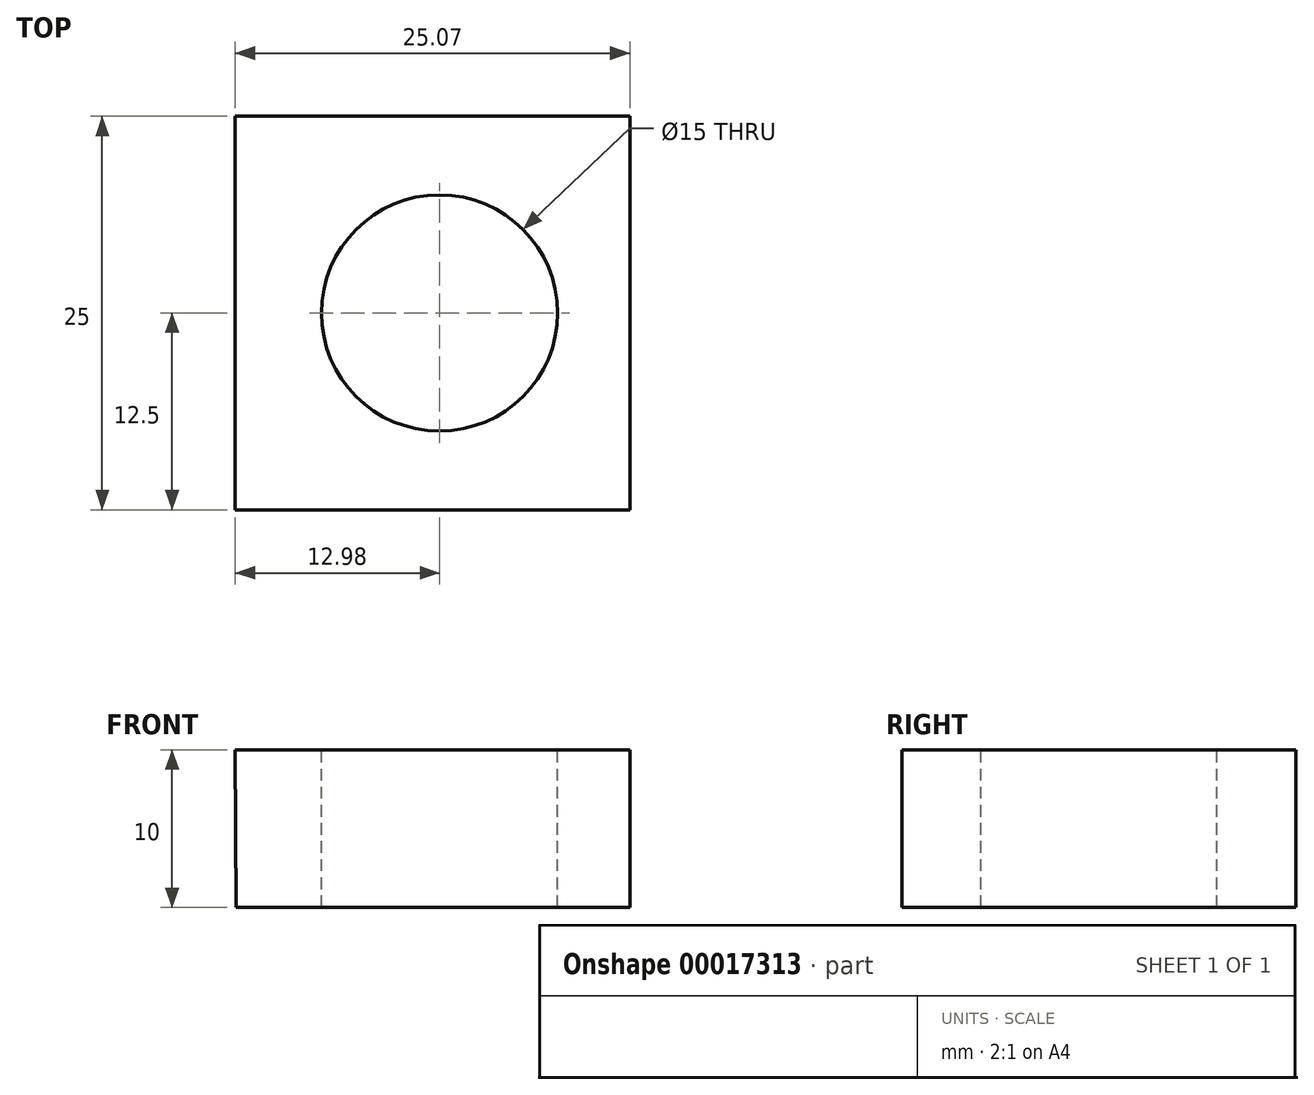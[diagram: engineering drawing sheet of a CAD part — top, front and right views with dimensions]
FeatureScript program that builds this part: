
annotation { "Feature Type Name" : "Feature", "Feature Type Description" : "" }
export const myFeature = defineFeature(function(context is Context, id is Id, definition is map)
    precondition{}
    {
        {
            var Q0;
            Q0=qCreatedBy(makeId("Front.planeOp"),FACE);
            var sketch = newSketch(context, id + "F0", { "sketchPlane" : qUnion([Q0])});
            skLineSegment(sketch, "E0", {"start": v(-12.9, -9.97) * mm, "end": v(12.1, -9.97) * mm});
            skLineSegment(sketch, "E1", {"start": v(12.1, 0.03) * mm, "end": v(-12.98, 0.03) * mm});
            skLineSegment(sketch, "E2", {"start": v(-12.98, 0.03) * mm, "end": v(-12.9, -9.97) * mm});
            skLineSegment(sketch, "E3", {"start": v(12.1, -9.97) * mm, "end": v(12.1, 0.03) * mm});
            skSolve(sketch);
        }
        {
            var Q0;
            Q0=makeQuery(id+"F0.imprint","IMPRINT",FACE,{"disambiguationData":[TD([[makeQuery(id+"F0.imprint","IMPRINT",EDGE,{"derivedFrom":sQuery(id+"F0.wireOp",EDGE,"E0")}),1.0]])]});
            extrude(context, id + "F1", {"entities" : qUnion([Q0]), "depth" : 25 * mm});
        }
        {
            var Q0;
            Q0=makeQuery(id+"F1.opExtrude","SWEPT_FACE",FACE,{"disambiguationData":[OSD([sQuery(id+"F0.wireOp",EDGE,"E1")])]});
            var sketch = newSketch(context, id + "F2", { "sketchPlane" : qUnion([Q0])});
            skCircle(sketch, "E4", {"center": v(0, -12.5) * mm, "radius": 7.5 * mm});
            skSolve(sketch);
        }
        {
            var Q0;
            Q0=makeQuery(id+"F2.imprint","IMPRINT",FACE,{"disambiguationData":[TD([[makeQuery(id+"F2.imprint","IMPRINT",EDGE,{"derivedFrom":sQuery(id+"F2.wireOp",EDGE,"E4")}),1.0]])]});
            extrude(context, id + "F3", {"entities" : qUnion([Q0]), "operationType" : NewBodyOperationType.REMOVE, "oppositeDirection" : true, "depth" : 10 * mm});
        }
    });
